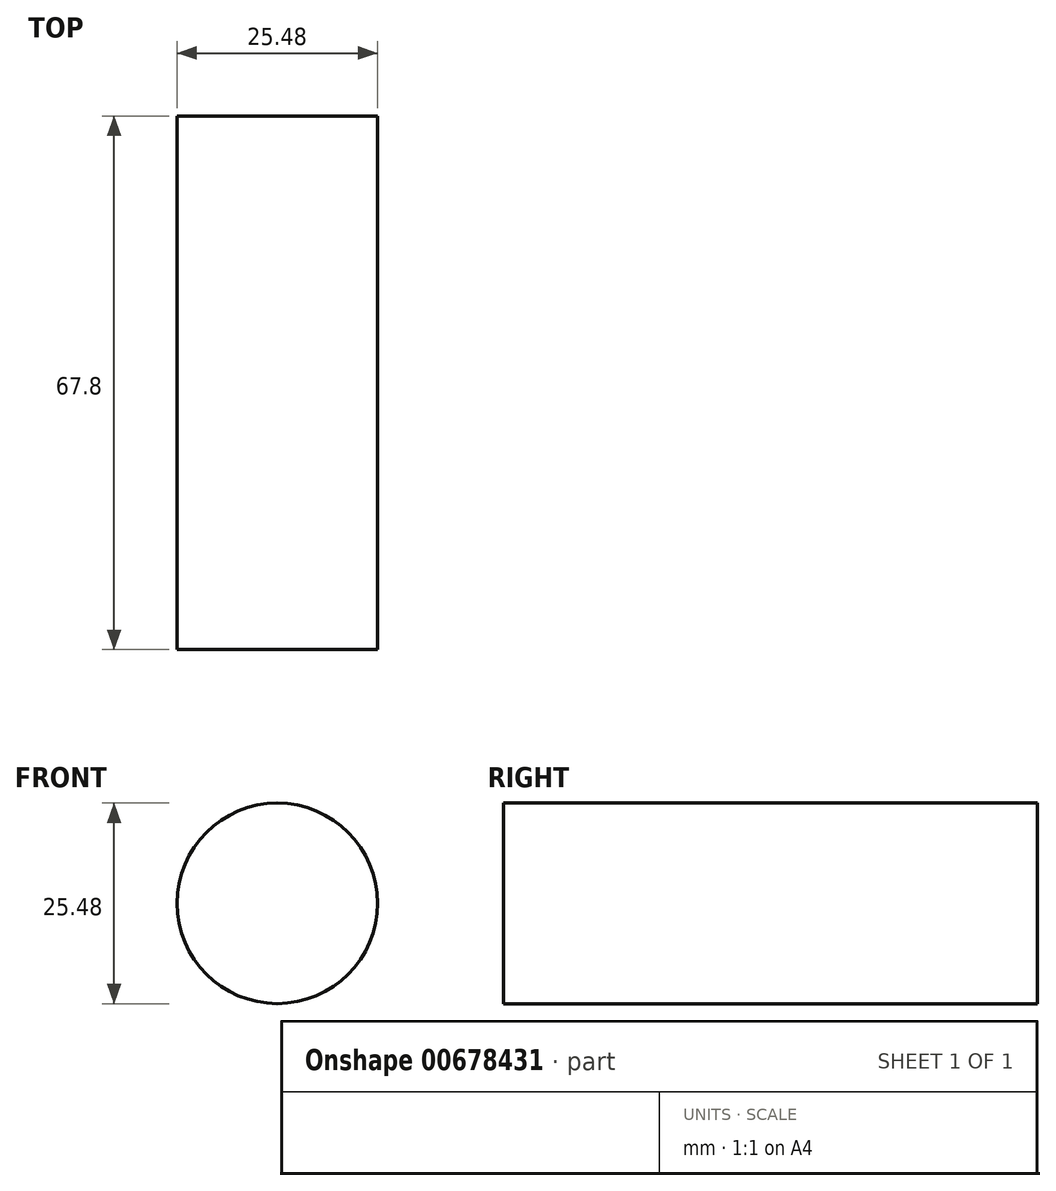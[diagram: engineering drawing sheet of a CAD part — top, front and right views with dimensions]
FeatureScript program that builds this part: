
annotation { "Feature Type Name" : "Feature", "Feature Type Description" : "" }
export const myFeature = defineFeature(function(context is Context, id is Id, definition is map)
    precondition{}
    {
        {
            var Q0;
            Q0=qCreatedBy(makeId("Front.planeOp"),FACE);
            var sketch = newSketch(context, id + "F0", { "sketchPlane" : qUnion([Q0])});
            skCircle(sketch, "E0", {"center": v(0, 0) * mm, "radius": 12.74 * mm});
            skSolve(sketch);
        }
        {
            var Q0;
            Q0 = qSketchRegion(id + "F0", true);
            extrude(context, id + "F1", {"entities" : qUnion([Q0]), "depth" : 67.8 * mm, "offsetDistance" : 25 * mm});
        }
    });
